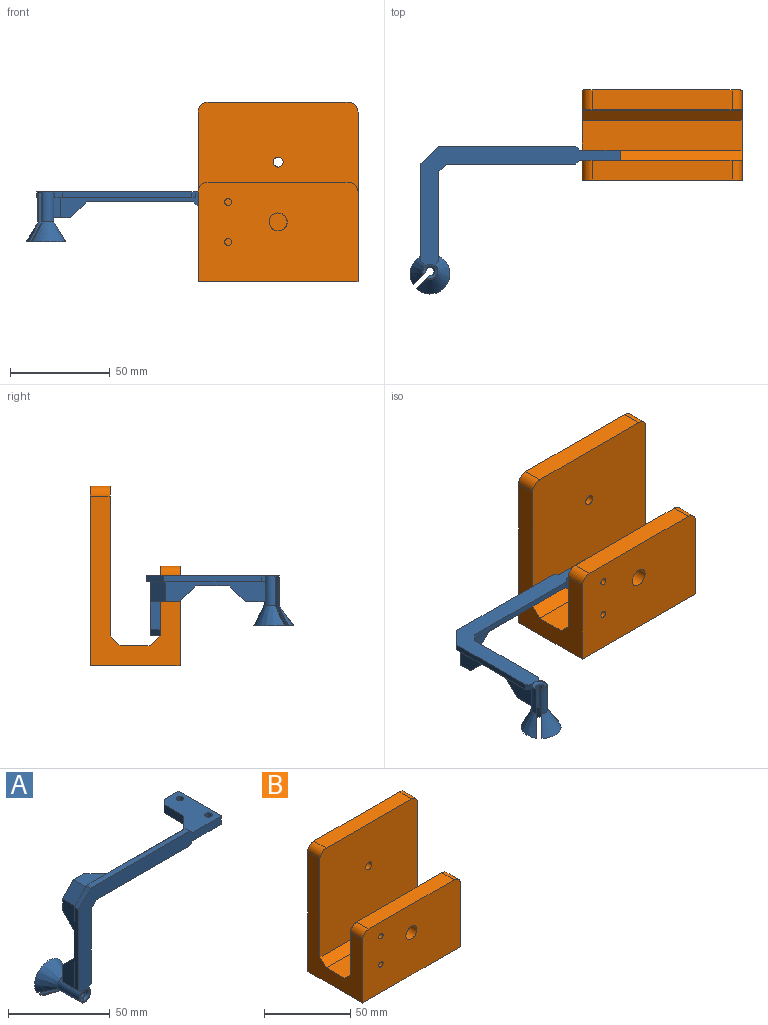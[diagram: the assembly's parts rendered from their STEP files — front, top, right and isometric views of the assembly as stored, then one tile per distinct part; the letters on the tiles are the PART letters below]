
ASSEMBLY  parts=2 mates=1
PART A: 41 faces, bbox 106.4x31.2x75.2 mm
  f0: plane 10x4.73mm, normal (0.71,0,-0.71), area 66.9mm2, adj f3,f16,f21,f32
  f1: plane 10x7.66mm, normal (-0.71,0,0.71), area 108.4mm2, adj f2,f15,f21,f40
  f2: plane 50x10mm, normal (-1,0,0), area 300.6mm2, adj f1,f4,f5,f20,f21,f24,f25,f40
  f3: plane 47.93x10mm, normal (1,0,0), area 279.9mm2, adj f0,f4,f5,f20,f21,f24,f25,f32
  f4: plane 16.93x5mm, normal (0,1,0), area 84.6mm2, adj f2,f3,f24,f25
  f5: cylinder r=4mm len=15mm, axis (0,-1,0), area 268.6mm2, adj f2,f3,f7,f9,f18,f19,f20,f34
  f6: plane 53.78x5mm, normal (0,1,0), area 268.9mm2, adj f15,f16,f22,f23
  f7: plane 99.66x66.79mm, normal (0,-1,0), area 1238.1mm2, adj f5,f11,f15,f16,f18,f19,f28,f29
  f8: cylinder r=2.05mm len=13.5mm, axis (0,-1,0), area 137.6mm2, adj f10,f18,f19,f28
  f9: bspline ~19.99x19.99mm, area 476.7mm2, adj f5,f17,f18,f19
  f10: bspline ~17x16.99mm, area 363.3mm2, adj f8,f17,f18,f19
  f11: plane 30x5mm, normal (1,0,0), area 150mm2, adj f7,f12,f15,f16
  f12: plane 10x5mm, normal (0,1,0), area 50mm2, adj f11,f13,f15,f16
  f13: plane 5x3.15mm, normal (-0.71,0.71,0), area 22.3mm2, adj f12,f14,f15,f16
  f14: plane 13.85x5mm, normal (-1,0,0), area 69.2mm2, adj f13,f15,f16,f22
  f15: plane 90x30mm, normal (0,0,1), area 665.1mm2, adj f1,f6,f7,f11,f12,f13,f14,f21
  f16: plane 87.93x30mm, normal (0,0,-1), area 644.4mm2, adj f0,f6,f7,f11,f12,f13,f14,f21
  f17: plane 20.04x20.04mm, normal (0,1,0), area 83.3mm2, adj f9,f10,f18,f19
  f18: plane 26.18x7.54mm, normal (0.71,0,-0.71), area 49.8mm2, adj f5,f7,f8,f9,f10,f17,f28
  f19: plane 25.14x6.66mm, normal (-0.71,0,0.71), area 49.3mm2, adj f5,f7,f8,f9,f10,f17,f28
  f20: plane 10x5mm, normal (0,1,0), area 47mm2, adj f2,f3,f5,f25
  f21: plane 14.73x14.73mm, normal (0,1,0), area 104.2mm2, adj f0,f1,f2,f3,f15,f16,f23,f24
  f22: plane 8x8mm, normal (-0.71,0.71,0), area 56.6mm2, adj f6,f14,f15,f16
  f23: plane 8x8mm, normal (0.71,0.71,0), area 56.6mm2, adj f6,f15,f16,f21
  f24: plane 8x8mm, normal (0,0.71,-0.71), area 56.6mm2, adj f2,f3,f4,f21
  f25: plane 8x8mm, normal (0,0.71,0.71), area 56.6mm2, adj f2,f3,f4,f20
  f26: cylinder r=1.78mm len=5mm, axis (0,0,-1), area 55.8mm2, adj f15,f16
  f27: cylinder r=1.78mm len=5mm, axis (0,0,-1), area 55.8mm2, adj f15,f16
  f28: torus R=3.55mm, axis (0,-1,0), area 32.4mm2, adj f7,f8,f18,f19
  f29: plane 45.1x3mm, normal (1,0,0), area 135.3mm2, adj f7,f30,f32,f34
  f30: plane 3.56x3.56mm, normal (0.71,0,-0.71), area 15.1mm2, adj f7,f29,f31,f32
  f31: plane 64.92x3mm, normal (0,0,-1), area 194.8mm2, adj f7,f30,f32,f33
  f32: plane 72.48x52.66mm, normal (0,1,0), area 237.4mm2, adj f0,f3,f16,f29,f30,f31,f33,f34
  f33: plane 3x2mm, normal (0.71,0,-0.71), area 8.5mm2, adj f7,f16,f31,f32
  f34: plane 3x2mm, normal (0.71,0,-0.71), area 8.5mm2, adj f5,f7,f29,f32
  f35: plane 3x2mm, normal (-0.71,0,-0.71), area 8.5mm2, adj f5,f7,f39,f40
  f36: plane 3x2mm, normal (0.71,0,0.71), area 8.5mm2, adj f7,f15,f37,f40
  f37: plane 68.65x3mm, normal (0,0,1), area 205.9mm2, adj f7,f36,f38,f40
  f38: plane 8.83x8.83mm, normal (-0.71,0,0.71), area 37.5mm2, adj f7,f37,f39,f40
  f39: plane 48.83x3mm, normal (-1,0,0), area 146.5mm2, adj f7,f35,f38,f40
  f40: plane 79.48x59.66mm, normal (0,1,0), area 260.6mm2, adj f1,f2,f15,f35,f36,f37,f38,f39
PART B: 23 faces, bbox 80x45x90 mm
  f0: plane 80x15mm, normal (0,0,1), area 1200mm2, adj f1,f4,f12,f15
  f1: plane 85x45mm, normal (1,0,0), area 1303mm2, adj f0,f5,f6,f7,f8,f10,f11,f12
  f2: cylinder r=2.5mm len=6.3mm, axis (0,-1,0), area 99mm2, adj f6,f8
  f3: plane 70x10mm, normal (0,0,1), area 700mm2, adj f6,f7,f21,f22
  f4: plane 85x45mm, normal (-1,0,0), area 1575mm2, adj f0,f5,f6,f7,f11,f12,f13,f15
  f5: plane 80x45mm, normal (0,0,-1), area 3402mm2, adj f1,f4,f7,f8,f9,f11
  f6: plane 80x75mm, normal (0,-1,0), area 5969.6mm2, adj f1,f2,f3,f4,f12,f21,f22
  f7: plane 90x80mm, normal (0,1,0), area 3257mm2, adj f1,f3,f4,f5,f9,f10,f21,f22
  f8: plane 73.5x53.5mm, normal (0,1,0), area 3912.6mm2, adj f1,f2,f5,f9,f10
  f9: plane 73.5x3.7mm, normal (1,0,0), area 272mm2, adj f5,f7,f8,f10
  f10: plane 53.5x3.7mm, normal (0,0,-1), area 198mm2, adj f1,f7,f8,f9
  f11: plane 80x50mm, normal (0,-1,0), area 3906.4mm2, adj f1,f4,f5,f14,f16,f17,f18,f19
  f12: plane 80x5mm, normal (0,-0.71,0.71), area 565.7mm2, adj f0,f1,f4,f6
  f13: plane 80x35mm, normal (0,1,0), area 2706.4mm2, adj f1,f4,f14,f15,f16,f17,f18,f19
  f14: plane 70x10mm, normal (0,0,1), area 700mm2, adj f11,f13,f19,f20
  f15: plane 80x5mm, normal (0,0.71,0.71), area 565.7mm2, adj f0,f1,f4,f13
  f16: cylinder r=1.75mm len=10mm, axis (0,-1,0), area 110mm2, adj f11,f13
  f17: cylinder r=1.75mm len=10mm, axis (0,-1,0), area 110mm2, adj f11,f13
  f18: cylinder r=4.5mm len=10mm, axis (0,-1,0), area 282.7mm2, adj f11,f13
  f19: cylinder r=5mm len=10mm, axis (0,-1,0), area 78.5mm2, adj f4,f11,f13,f14
  f20: cylinder r=5mm len=10mm, axis (0,1,0), area 78.5mm2, adj f1,f11,f13,f14
  f21: cylinder r=5mm len=10mm, axis (0,1,0), area 78.5mm2, adj f1,f3,f6,f7
  f22: cylinder r=5mm len=10mm, axis (0,-1,0), area 78.5mm2, adj f3,f4,f6,f7
PLACE A rot(axis=(-1,0,0),90deg) t=(-36,-25,-20)mm
PLACE B t=(0,10,0)mm
MATE fastened A.f27 <-> B.f17  axis (0,-1,0) through (-25,-25,-20)mm
